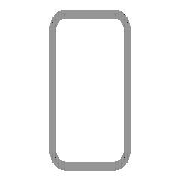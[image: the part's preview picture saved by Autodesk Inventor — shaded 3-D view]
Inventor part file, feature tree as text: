
AUTODESK INVENTOR PART (.ipt)
format: ipt  version: 2025.3 (Build 293356030, 356C)  size: 149,504 bytes
history: native  units: mm (DEFAULTED — no unit token found)
features: other x4, plane x3, split x2, sketch x1
ambient origin geometry x8: Origin, YZ Plane, XZ Plane, XY Plane, X Axis, Y Axis, Z Axis, Center Point
bodies: Solid1 (feature_tree), Body (feature_tree)
feature tree (10):
  parser-record x1  (decoder bookkeeping rows leaked as tree rows — omitted from the tree; the rows remain in map.json)
  other  "Driven Length"
  other  "Start Plane"
  other  "End Plane"
  plane  "Work Plane4"
  split  "Split1"
  plane  "Work Plane5"
  split  "Split2"
  sketch  "Sketch3"  dims[d3=926.934633mm d4=0.0mm d7=6.0mm d9=40.0mm d11=80.0mm d12=3.0mm d13=149.66701mm d14=1076.601644mm d15=20.0mm d16=40.0mm d17=90.0deg d18=926.934633mm]
  plane  "Work Plane3"
